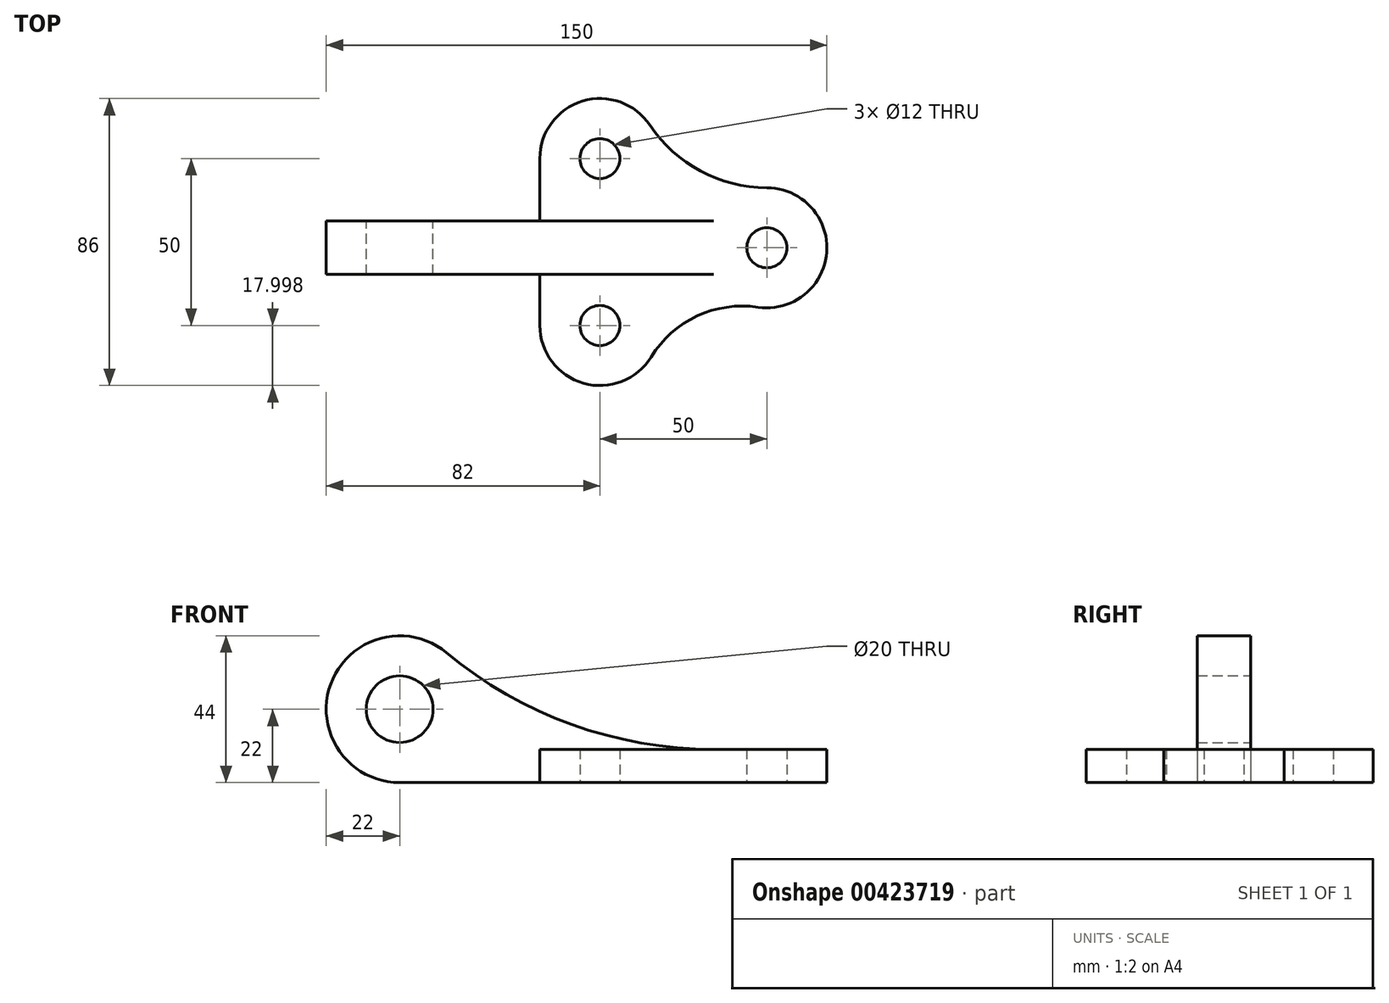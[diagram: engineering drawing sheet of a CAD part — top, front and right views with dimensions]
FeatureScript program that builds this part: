
annotation { "Feature Type Name" : "Feature", "Feature Type Description" : "" }
export const myFeature = defineFeature(function(context is Context, id is Id, definition is map)
    precondition{}
    {
        {
            var Q0;
            Q0=qCreatedBy(makeId("Top.planeOp"),FACE);
            var sketch = newSketch(context, id + "F0", { "sketchPlane" : qUnion([Q0])});
            skCircle(sketch, "E0", {"center": v(0, 0) * mm, "radius": 6 * mm});
            skArc(sketch, "E1", {"start": v(-2.63, -17.8) * mm, "mid": v(17.95, -1.32) * mm, "end": v(0, 18) * mm});
            skCircle(sketch, "E2", {"center": v(-50, 26.72) * mm, "radius": 6 * mm});
            skArc(sketch, "E3", {"start": v(-35.04, 36.72) * mm, "mid": v(-55.23, 43.94) * mm, "end": v(-68, 26.72) * mm});
            skCircle(sketch, "E4", {"center": v(-50, -23.28) * mm, "radius": 6 * mm});
            skArc(sketch, "E5", {"start": v(-68, -23.28) * mm, "mid": v(-54.9, -40.6) * mm, "end": v(-34.68, -32.73) * mm});
            skLineSegment(sketch, "E6", {"start": v(-68, 26.72) * mm, "end": v(-68, -23.28) * mm});
            skArc(sketch, "E7", {"start": v(-35.04, 36.72) * mm, "mid": v(-19.86, 22.97) * mm, "end": v(0, 18) * mm});
            skArc(sketch, "E8", {"start": v(-2.63, -17.8) * mm, "mid": v(-20.9, -20.46) * mm, "end": v(-34.68, -32.73) * mm});
            skSolve(sketch);
        }
        {
            var Q0;
            Q0=makeQuery(id+"F0.imprint","IMPRINT",FACE,{"disambiguationData":[TD([[makeQuery(id+"F0.imprint","IMPRINT",EDGE,{"derivedFrom":sQuery(id+"F0.wireOp",EDGE,"E0")}),-1.0]])]});
            extrude(context, id + "F1", {"entities" : qUnion([Q0]), "depth" : 10 * mm});
        }
        {
            var Q0;
            Q0=qCreatedBy(makeId("Front.planeOp"),FACE);
            var sketch = newSketch(context, id + "F2", { "sketchPlane" : qUnion([Q0])});
            skCircle(sketch, "E9", {"center": v(-110, 22) * mm, "radius": 10 * mm});
            skArc(sketch, "E10", {"start": v(-95.93, 38.91) * mm, "mid": v(-130.69, 29.48) * mm, "end": v(-110, 0) * mm});
            skLineSegment(sketch, "E11.0.0", {"start": v(-68, 0) * mm, "end": v(-34.68, 0) * mm, "construction": true});
            skLineSegment(sketch, "E11.0.1", {"start": v(-34.68, 0) * mm, "end": v(-34.68, 10) * mm, "construction": true});
            skLineSegment(sketch, "E11.0.2", {"start": v(-34.68, 10) * mm, "end": v(-68, 10) * mm, "construction": true});
            skLineSegment(sketch, "E11.0.3", {"start": v(-68, 10) * mm, "end": v(-68, 0) * mm, "construction": true});
            skLineSegment(sketch, "E12", {"start": v(-68, 0) * mm, "end": v(-72.56, 0) * mm, "construction": true});
            skLineSegment(sketch, "E13", {"start": v(-162.35, 0) * mm, "end": v(-68, 0) * mm, "construction": true});
            skLineSegment(sketch, "E14", {"start": v(-110, 0) * mm, "end": v(-15.98, 0) * mm});
            skArc(sketch, "E15", {"start": v(-95.93, 38.91) * mm, "mid": v(-58.49, 17.45) * mm, "end": v(-15.98, 10) * mm});
            skLineSegment(sketch, "E16", {"start": v(-15.98, 10) * mm, "end": v(-15.98, 0) * mm});
            skSolve(sketch);
        }
        {
            var Q0;
            Q0=makeQuery(id+"F2.imprint","IMPRINT",FACE,{"disambiguationData":[TD([[makeQuery(id+"F2.imprint","IMPRINT",EDGE,{"derivedFrom":sQuery(id+"F2.wireOp",EDGE,"E9")}),-1.0]])]});
            extrude(context, id + "F3", {"entities" : qUnion([Q0]), "operationType" : NewBodyOperationType.ADD, "depth" : 8 * mm, "hasSecondDirection" : true, "secondDirectionOppositeDirection" : true, "secondDirectionDepth" : 8 * mm});
        }
    });
